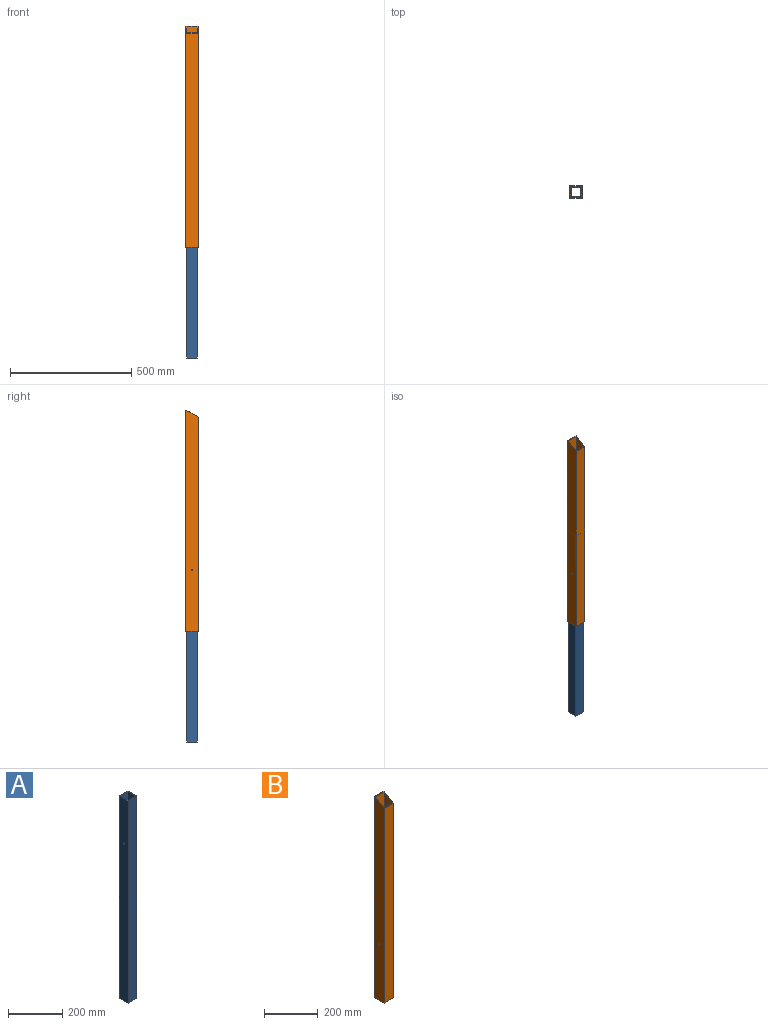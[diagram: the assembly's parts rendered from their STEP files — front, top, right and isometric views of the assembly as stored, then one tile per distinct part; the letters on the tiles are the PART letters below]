
ASSEMBLY  parts=2 mates=1
PART A: 12 faces, bbox 44.5x44.5x914.4 mm
  f0: plane 914.4x44.45mm, normal (0,-1,0), area 40645.1mm2, adj f1,f7,f8,f9
  f1: plane 914.4x44.45mm, normal (1,0,0), area 40613.4mm2, adj f0,f2,f8,f9,f11
  f2: plane 914.4x44.45mm, normal (0,1,0), area 40645.1mm2, adj f1,f7,f8,f9
  f3: plane 914.4x38.35mm, normal (-1,0,0), area 35039.2mm2, adj f4,f6,f8,f9,f11
  f4: plane 914.4x38.35mm, normal (0,1,0), area 35070.9mm2, adj f3,f5,f8,f9
  f5: plane 914.4x38.35mm, normal (1,0,0), area 35039.2mm2, adj f4,f6,f8,f9,f10
  f6: plane 914.4x38.35mm, normal (0,-1,0), area 35070.9mm2, adj f3,f5,f8,f9
  f7: plane 914.4x44.45mm, normal (-1,0,0), area 40613.4mm2, adj f0,f2,f8,f9,f10
  f8: plane 44.45x44.45mm, normal (0,0,1), area 504.8mm2, adj f0,f1,f2,f3,f4,f5,f6,f7
  f9: plane 44.45x44.45mm, normal (0,0,-1), area 504.8mm2, adj f0,f1,f2,f3,f4,f5,f6,f7
  f10: cylinder r=3.17mm len=6.35mm, axis (-1,0,0), area 60.8mm2, adj f5,f7
  f11: cylinder r=3.17mm len=6.35mm, axis (-1,0,0), area 60.8mm2, adj f1,f3
PART B: 12 faces, bbox 50.8x50.8x914.4 mm
  f0: plane 885.07x50.8mm, normal (0,-1,0), area 44961.6mm2, adj f1,f7,f8,f10
  f1: plane 914.4x50.8mm, normal (1,0,0), area 45674.9mm2, adj f0,f2,f8,f10,f11
  f2: plane 914.4x50.8mm, normal (0,1,0), area 46451.5mm2, adj f1,f7,f8,f10
  f3: plane 912.64x44.7mm, normal (-1,0,0), area 40190.1mm2, adj f4,f6,f8,f10,f11
  f4: plane 886.83x44.7mm, normal (0,1,0), area 39644.9mm2, adj f3,f5,f8,f10
  f5: plane 912.64x44.7mm, normal (1,0,0), area 40190.1mm2, adj f4,f6,f8,f9,f10
  f6: plane 912.64x44.7mm, normal (0,-1,0), area 40798.7mm2, adj f3,f5,f8,f10
  f7: plane 914.4x50.8mm, normal (-1,0,0), area 45674.9mm2, adj f0,f2,f8,f9,f10
  f8: plane 50.8x50.8mm, normal (0,0,-1), area 582.2mm2, adj f0,f1,f2,f3,f4,f5,f6,f7
  f9: cylinder r=3.17mm len=6.35mm, axis (-1,0,0), area 60.8mm2, adj f5,f7
  f10: plane 50.8x50.8mm, normal (0,-0.5,0.87), area 672.3mm2, adj f0,f1,f2,f3,f4,f5,f6,f7
  f11: cylinder r=3.17mm len=6.35mm, axis (-1,0,0), area 60.8mm2, adj f1,f3
PLACE A t=(-67.82,-62.1,-34.41)mm
PLACE B t=(-67.7,-62.1,422.79)mm
MATE fastened B.f9 <-> A.f10  axis (-1,0,0) through (-93.1,-62.1,219.59)mm
